# Revit family: Outdoor-Kitchen-Cabinets_Kalamazoo_Storage-Cabinets_Signature1
name_source: partatom
category: Specialty Equipment
revit_build: Autodesk Revit 2018 (Build: 20190510_1515(x64)
units: mm (PartAtom-declared; Revit-internal decimal feet)

## family parameters
Always vertical = Yes
Cut with Voids When Loaded = No
OmniClass Number = 23.40.40.11
OmniClass Title = Specialized Food Storage and Display Furnishings
Part Type = Normal
Room Calculation Point = No
Round Connector Dimension = Use Diameter
Shared = No
Work Plane-Based = No

## types (1)
- Load Type Catalog
    Assembly Code = E1090310
    Depth = 30"
    Description = Signature 18-inch Outdoor Base Cabinet - 3 Drawers
    Edition number = 1
    I_Base = Yes
    I_Base_K-RY-PO = No
    I_Frame = Yes
    I_Handle_K-RY-PO = No
    I_Handle_K-STOR-24-L = No
    I_K-3DRW = Yes
    I_K-OSHC-27 = No
    I_K-RY-PO = No
    I_K-STOR-30-36 = No
    Keynote = 11400
    Manufacturer = Kalamazoo Outdoor Gourmet
    Model = K-3DRW-18
    Product Guid = 3f1309b6-a32a-4e54-9983-35f482e8884d
    Product Material = Kalamazoo - Stainless Steel - 304 OR 316L
    Product data url = https://www.bimobject.com
    URL = https://kalamazoogourmet.com
    Weight (lb) = 190.00 lbf
    Width = 18"
    Ι_Gnrc Mdl Optn 01 = Extension : +3/4"
    Ι_Gnrc Mdl Optn 02 = Extension : -3/4"

## geometry (parser evidence)
native form markers: Sweep x12
no freeform markers — native parametric forms only
